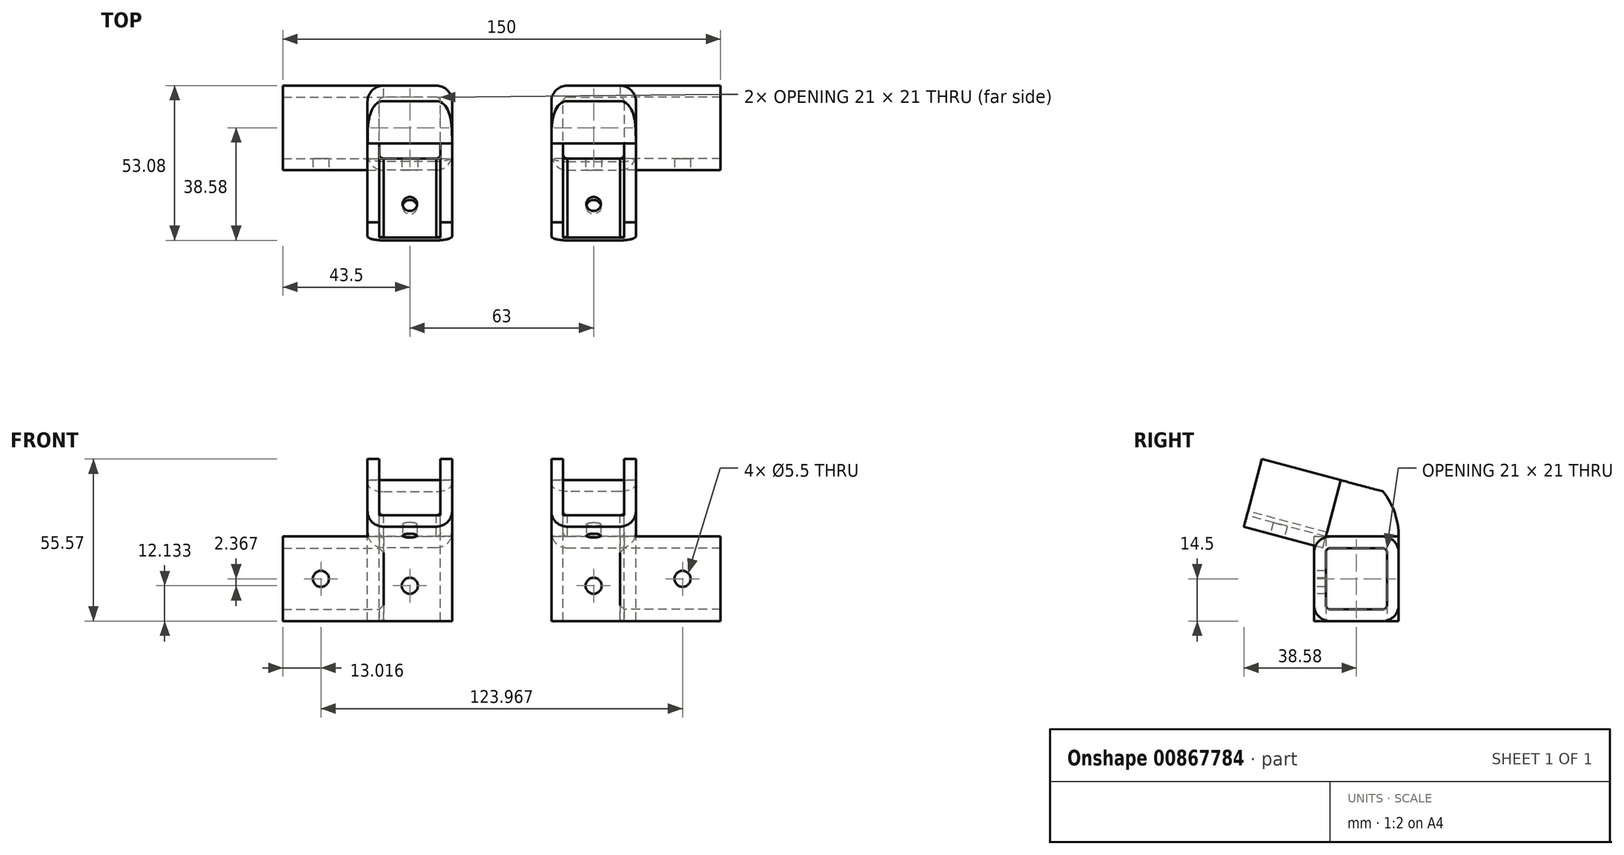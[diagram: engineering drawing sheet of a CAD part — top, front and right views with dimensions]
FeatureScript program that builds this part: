
annotation { "Feature Type Name" : "Feature", "Feature Type Description" : "" }
export const myFeature = defineFeature(function(context is Context, id is Id, definition is map)
    precondition{}
    {
        {
            var Q0;
            Q0=qCreatedBy(makeId("Top.planeOp"),FACE);
            var sketch = newSketch(context, id + "F0", { "sketchPlane" : qUnion([Q0])});
            skLineSegment(sketch, "E0.bottom", {"start": v(1.5, 0) * mm, "end": v(19.5, 0) * mm});
            skLineSegment(sketch, "E0.top", {"start": v(1.5, 21) * mm, "end": v(19.5, 21) * mm});
            skLineSegment(sketch, "E0.left", {"start": v(0, 1.5) * mm, "end": v(0, 19.5) * mm});
            skLineSegment(sketch, "E0.right", {"start": v(21, 1.5) * mm, "end": v(21, 19.5) * mm});
            skPoint(sketch, "E1.visualSharp", {"position": v(21, 21) * mm});
            skArc(sketch, "E1.filletArc", {"start": v(21, 19.5) * mm, "mid": v(20.56, 20.56) * mm, "end": v(19.5, 21) * mm});
            skPoint(sketch, "E2.visualSharp", {"position": v(21, 0) * mm});
            skArc(sketch, "E2.filletArc", {"start": v(19.5, 0) * mm, "mid": v(20.56, 0.44) * mm, "end": v(21, 1.5) * mm});
            skPoint(sketch, "E3.visualSharp", {"position": v(0, 0) * mm});
            skArc(sketch, "E3.filletArc", {"start": v(0, 1.5) * mm, "mid": v(0.44, 0.44) * mm, "end": v(1.5, 0) * mm});
            skPoint(sketch, "E4.visualSharp", {"position": v(0, 21) * mm});
            skArc(sketch, "E4.filletArc", {"start": v(1.5, 21) * mm, "mid": v(0.44, 20.56) * mm, "end": v(0, 19.5) * mm});
            skArc(sketch, "E5.0", {"start": v(19.5, -4) * mm, "mid": v(23.39, -2.39) * mm, "end": v(25, 1.5) * mm});
            skLineSegment(sketch, "E5.1", {"start": v(1.5, -4) * mm, "end": v(19.5, -4) * mm});
            skLineSegment(sketch, "E5.2", {"start": v(25, 1.5) * mm, "end": v(25, 19.5) * mm});
            skArc(sketch, "E5.3", {"start": v(-4, 1.5) * mm, "mid": v(-2.39, -2.39) * mm, "end": v(1.5, -4) * mm});
            skArc(sketch, "E5.4", {"start": v(25, 19.5) * mm, "mid": v(23.39, 23.39) * mm, "end": v(19.5, 25) * mm});
            skLineSegment(sketch, "E5.5", {"start": v(1.5, 25) * mm, "end": v(19.5, 25) * mm});
            skArc(sketch, "E5.6", {"start": v(1.5, 25) * mm, "mid": v(-2.39, 23.39) * mm, "end": v(-4, 19.5) * mm});
            skLineSegment(sketch, "E5.7", {"start": v(-4, 1.5) * mm, "end": v(-4, 19.5) * mm});
            skSolve(sketch);
        }
        {
            var Q0;
            Q0=makeQuery(id+"F0.imprint","IMPRINT",FACE,{"disambiguationData":[TD([[makeQuery(id+"F0.imprint","IMPRINT",EDGE,{"derivedFrom":sQuery(id+"F0.wireOp",EDGE,"E0.bottom")}),-1.0]])]});
            extrude(context, id + "F1", {"entities" : qUnion([Q0]), "oppositeDirection" : true, "depth" : 29 * mm, "offsetDistance" : 25 * mm});
        }
        {
            var Q0;
            Q0=qCreatedBy(makeId("Right.planeOp"),FACE);
            var sketch = newSketch(context, id + "F2", { "sketchPlane" : qUnion([Q0])});
            skLineSegment(sketch, "E6", {"start": v(0, 0) * mm, "end": v(-27.05, 7.25) * mm});
            skLineSegment(sketch, "E7", {"start": v(-27.05, 7.25) * mm, "end": v(-21.87, 26.57) * mm});
            skLineSegment(sketch, "E8", {"start": v(-21.87, 26.57) * mm, "end": v(5.18, 19.32) * mm});
            skLineSegment(sketch, "E9", {"start": v(5.18, 19.32) * mm, "end": v(0, 0) * mm});
            skSolve(sketch);
        }
        {
            var Q0;
            Q0=makeQuery(id+"F2.imprint","IMPRINT",FACE,{"disambiguationData":[TD([[makeQuery(id+"F2.imprint","IMPRINT",EDGE,{"derivedFrom":sQuery(id+"F2.wireOp",EDGE,"E6")}),-1.0]])]});
            extrude(context, id + "F3", {"entities" : qUnion([Q0]), "depth" : 21 * mm, "offsetDistance" : 25 * mm});
        }
        {
            var Q0;
            Q0=makeQuery(id+"F3.opExtrude","SWEPT_FACE",FACE,{"disambiguationData":[OSD([sQuery(id+"F2.wireOp",EDGE,"E7")])]});
            var sketch = newSketch(context, id + "F4", { "sketchPlane" : qUnion([Q0])});
            skLineSegment(sketch, "E10", {"start": v(0, 20) * mm, "end": v(0, 1.5) * mm});
            skLineSegment(sketch, "E11", {"start": v(1.5, 0) * mm, "end": v(19.5, 0) * mm});
            skLineSegment(sketch, "E12", {"start": v(21, 1.5) * mm, "end": v(21, 20) * mm});
            skPoint(sketch, "E13.visualSharp", {"position": v(0, 0) * mm});
            skArc(sketch, "E13.filletArc", {"start": v(0, 1.5) * mm, "mid": v(0.44, 0.44) * mm, "end": v(1.5, 0) * mm});
            skPoint(sketch, "E14.visualSharp", {"position": v(21, 0) * mm});
            skArc(sketch, "E14.filletArc", {"start": v(19.5, 0) * mm, "mid": v(20.56, 0.44) * mm, "end": v(21, 1.5) * mm});
            skLineSegment(sketch, "E15.0", {"start": v(25, 1.5) * mm, "end": v(25, 20) * mm});
            skLineSegment(sketch, "E15.1", {"start": v(-4, 20) * mm, "end": v(-4, 1.5) * mm});
            skArc(sketch, "E15.2", {"start": v(-4, 1.5) * mm, "mid": v(-2.39, -2.39) * mm, "end": v(1.5, -4) * mm});
            skLineSegment(sketch, "E15.3", {"start": v(1.5, -4) * mm, "end": v(19.5, -4) * mm});
            skArc(sketch, "E15.4", {"start": v(19.5, -4) * mm, "mid": v(23.39, -2.39) * mm, "end": v(25, 1.5) * mm});
            skLineSegment(sketch, "E16", {"start": v(-4, 20) * mm, "end": v(0, 20) * mm});
            skLineSegment(sketch, "E17", {"start": v(21, 20) * mm, "end": v(25, 20) * mm});
            skSolve(sketch);
        }
        {
            var Q0;
            {var subQ0=sQuery(id+"F4.wireOp",EDGE,"E10");Q0=makeQuery(id+"F4.imprint","IMPRINT",FACE,{"disambiguationData":[TD([[makeQuery(id+"F4.imprint","IMPRINT",EDGE,{"derivedFrom":subQ0}),1.0]])]});}
            extrude(context, id + "F5", {"entities" : qUnion([Q0]), "oppositeDirection" : true, "depth" : 28 * mm, "offsetDistance" : 25 * mm});
        }
        {
            var Q0;
            Q0=makeQuery(id+"F5.opExtrude","CAP_FACE",FACE,{"disambiguationData":[OSD([sQuery(id+"F2.wireOp",EDGE,"E6"),sQuery(id+"F2.wireOp",EDGE,"E7"),sQuery(id+"F4.wireOp",EDGE,"E10"),sQuery(id+"F4.wireOp",EDGE,"E11"),sQuery(id+"F4.wireOp",EDGE,"E12"),sQuery(id+"F4.wireOp",EDGE,"E15.0"),sQuery(id+"F4.wireOp",EDGE,"E15.1"),sQuery(id+"F4.wireOp",EDGE,"E15.2"),sQuery(id+"F4.wireOp",EDGE,"E15.3"),sQuery(id+"F4.wireOp",EDGE,"E15.4"),sQuery(id+"F4.wireOp",EDGE,"E16"),sQuery(id+"F4.wireOp",EDGE,"E17")])],"isStart":true});
            var sketch = newSketch(context, id + "F6", { "sketchPlane" : qUnion([Q0])});
            skLineSegment(sketch, "E18.bottom", {"start": v(0, 20) * mm, "end": v(21, 20) * mm});
            skLineSegment(sketch, "E18.top", {"start": v(1.5, 0) * mm, "end": v(19.5, 0) * mm});
            skLineSegment(sketch, "E18.left", {"start": v(0, 20) * mm, "end": v(0, 1.5) * mm});
            skLineSegment(sketch, "E18.right", {"start": v(21, 20) * mm, "end": v(21, 1.5) * mm});
            skPoint(sketch, "E19.visualSharp", {"position": v(0, 0) * mm});
            skArc(sketch, "E19.filletArc", {"start": v(0, 1.5) * mm, "mid": v(0.44, 0.44) * mm, "end": v(1.5, 0) * mm});
            skPoint(sketch, "E20.visualSharp", {"position": v(21, 0) * mm});
            skArc(sketch, "E20.filletArc", {"start": v(19.5, 0) * mm, "mid": v(20.56, 0.44) * mm, "end": v(21, 1.5) * mm});
            skSolve(sketch);
        }
        {
            var Q0;
            Q0=makeQuery(id+"F6.imprint","IMPRINT",FACE,{"disambiguationData":[TD([[makeQuery(id+"F6.imprint","IMPRINT",EDGE,{"derivedFrom":sQuery(id+"F6.wireOp",EDGE,"E18.bottom")}),-1.0]])]});
            extrude(context, id + "F7", {"entities" : qUnion([Q0]), "operationType" : NewBodyOperationType.REMOVE, "oppositeDirection" : true, "depth" : 28 * mm, "offsetDistance" : 25 * mm});
        }
        {
            var Q0;
            Q0=makeQuery(id+"F1.opExtrude","CAP_FACE",FACE,{"disambiguationData":[OSD([sQuery(id+"F0.wireOp",EDGE,"E0.bottom"),sQuery(id+"F0.wireOp",EDGE,"E0.top"),sQuery(id+"F0.wireOp",EDGE,"E0.left"),sQuery(id+"F0.wireOp",EDGE,"E0.right"),sQuery(id+"F0.wireOp",EDGE,"E1.filletArc"),sQuery(id+"F0.wireOp",EDGE,"E2.filletArc"),sQuery(id+"F0.wireOp",EDGE,"E3.filletArc"),sQuery(id+"F0.wireOp",EDGE,"E4.filletArc"),sQuery(id+"F0.wireOp",EDGE,"E5.0"),sQuery(id+"F0.wireOp",EDGE,"E5.1"),sQuery(id+"F0.wireOp",EDGE,"E5.2"),sQuery(id+"F0.wireOp",EDGE,"E5.3"),sQuery(id+"F0.wireOp",EDGE,"E5.4"),sQuery(id+"F0.wireOp",EDGE,"E5.5"),sQuery(id+"F0.wireOp",EDGE,"E5.6"),sQuery(id+"F0.wireOp",EDGE,"E5.7")])],"isStart":true});
            var sketch = newSketch(context, id + "F8", { "sketchPlane" : qUnion([Q0])});
            skLineSegment(sketch, "E21.bottom", {"start": v(1.5, 21) * mm, "end": v(19.5, 21) * mm});
            skLineSegment(sketch, "E21.top", {"start": v(1.5, 0) * mm, "end": v(19.5, 0) * mm});
            skLineSegment(sketch, "E21.left", {"start": v(0, 19.5) * mm, "end": v(0, 1.5) * mm});
            skLineSegment(sketch, "E21.right", {"start": v(21, 19.5) * mm, "end": v(21, 1.5) * mm});
            skPoint(sketch, "E22.visualSharp", {"position": v(21, 21) * mm});
            skArc(sketch, "E22.filletArc", {"start": v(21, 19.5) * mm, "mid": v(20.56, 20.56) * mm, "end": v(19.5, 21) * mm});
            skPoint(sketch, "E23.visualSharp", {"position": v(0, 21) * mm});
            skArc(sketch, "E23.filletArc", {"start": v(1.5, 21) * mm, "mid": v(0.44, 20.56) * mm, "end": v(0, 19.5) * mm});
            skPoint(sketch, "E24.visualSharp", {"position": v(0, 0) * mm});
            skArc(sketch, "E24.filletArc", {"start": v(0, 1.5) * mm, "mid": v(0.44, 0.44) * mm, "end": v(1.5, 0) * mm});
            skPoint(sketch, "E25.visualSharp", {"position": v(21, 0) * mm});
            skArc(sketch, "E25.filletArc", {"start": v(19.5, 0) * mm, "mid": v(20.56, 0.44) * mm, "end": v(21, 1.5) * mm});
            skArc(sketch, "E26.0", {"start": v(19.5, -4) * mm, "mid": v(23.39, -2.39) * mm, "end": v(25, 1.5) * mm});
            skLineSegment(sketch, "E26.1", {"start": v(25, 19.5) * mm, "end": v(25, 1.5) * mm});
            skArc(sketch, "E26.2", {"start": v(25, 19.5) * mm, "mid": v(23.39, 23.39) * mm, "end": v(19.5, 25) * mm});
            skArc(sketch, "E26.3", {"start": v(-4, 1.5) * mm, "mid": v(-2.39, -2.39) * mm, "end": v(1.5, -4) * mm});
            skLineSegment(sketch, "E26.4", {"start": v(-4, 19.5) * mm, "end": v(-4, 1.5) * mm});
            skArc(sketch, "E26.5", {"start": v(1.5, 25) * mm, "mid": v(-2.39, 23.39) * mm, "end": v(-4, 19.5) * mm});
            skLineSegment(sketch, "E26.6", {"start": v(1.5, 25) * mm, "end": v(19.5, 25) * mm});
            skLineSegment(sketch, "E27", {"start": v(24.8, 0) * mm, "end": v(-3.8, 0) * mm});
            skSolve(sketch);
        }
        {
            var Q0;
            Q0=makeQuery(id+"F8.imprint","IMPRINT",FACE,{"disambiguationData":[TD([[makeQuery(id+"F8.imprint","IMPRINT",EDGE,{"derivedFrom":sQuery(id+"F8.wireOp",EDGE,"E21.bottom")}),1.0]])]});
            var Q1;
            Q1=makeQuery(id+"F8.imprint","IMPRINT",FACE,{"disambiguationData":[TD([[makeQuery(id+"F8.imprint","IMPRINT",EDGE,{"derivedFrom":sQuery(id+"F8.wireOp",EDGE,"E21.bottom")}),-1.0]])]});
            var Q2;
            Q2=sQuery(id+"F8.wireOp",EDGE,"E21.top");
            revolve(context, id + "F9", {"surfaceOperationType" : NewSurfaceOperationType.NEW, "entities" : qUnion([Q0, Q1]), "axis" : qUnion([Q2]), "revolveType" : RevolveType.ONE_DIRECTION, "angle" : 75 * degree});
        }
        {
            var Q0;
            Q0=makeQuery(id+"F9.opRevolve","SWEPT_FACE",FACE,{"disambiguationData":[OSD([sQuery(id+"F8.wireOp",EDGE,"E26.4")])]});
            var sketch = newSketch(context, id + "F10", { "sketchPlane" : qUnion([Q0])});
            skLineSegment(sketch, "E28", {"start": v(-5.05, 18.84) * mm, "end": v(-5.18, 19.32) * mm});
            skLineSegment(sketch, "E29", {"start": v(-5.18, 19.32) * mm, "end": v(-21.6, 14.92) * mm});
            skLineSegment(sketch, "E30", {"start": v(-21.6, 14.92) * mm, "end": v(-23.5, 23.3) * mm});
            skLineSegment(sketch, "E31", {"start": v(-23.5, 23.3) * mm, "end": v(-5.18, 24.55) * mm});
            skLineSegment(sketch, "E32", {"start": v(-5.18, 24.55) * mm, "end": v(-5.18, 19.32) * mm});
            skSolve(sketch);
        }
        {
            var Q0;
            Q0=makeQuery(id+"F10.imprint","IMPRINT",FACE,{"disambiguationData":[TD([[makeQuery(id+"F10.imprint","IMPRINT",EDGE,{"derivedFrom":sQuery(id+"F10.wireOp",EDGE,"E29")}),-1.0]])]});
            extrude(context, id + "F11", {"entities" : qUnion([Q0]), "operationType" : NewBodyOperationType.REMOVE, "oppositeDirection" : true, "depth" : 43.3 * mm, "offsetDistance" : 25 * mm});
        }
        {
            var Q0;
            Q0=makeQuery(id+"F1.opExtrude","SWEPT_FACE",FACE,{"disambiguationData":[OSD([sQuery(id+"F0.wireOp",EDGE,"E5.1")])]});
            var sketch = newSketch(context, id + "F12", { "sketchPlane" : qUnion([Q0])});
            skCircle(sketch, "E33", {"center": v(10.5, -16.87) * mm, "radius": 2.75 * mm});
            skPoint(sketch, "E33.centerSnap0", {"position": v(10.5, -29) * mm});
            skSolve(sketch);
        }
        {
            var Q0;
            Q0=makeQuery(id+"F12.imprint","IMPRINT",FACE,{"disambiguationData":[TD([[makeQuery(id+"F12.imprint","IMPRINT",EDGE,{"derivedFrom":sQuery(id+"F12.wireOp",EDGE,"E33")}),1.0]])]});
            extrude(context, id + "F13", {"entities" : qUnion([Q0]), "operationType" : NewBodyOperationType.REMOVE, "oppositeDirection" : true, "depth" : 5 * mm, "offsetDistance" : 25 * mm});
        }
        {
            var Q0;
            Q0=makeQuery(id+"F5.opExtrude","SWEPT_FACE",FACE,{"disambiguationData":[OSD([sQuery(id+"F4.wireOp",EDGE,"E15.3")])]});
            var sketch = newSketch(context, id + "F14", { "sketchPlane" : qUnion([Q0])});
            skCircle(sketch, "E34", {"center": v(10.5, 16.15) * mm, "radius": 2.5 * mm});
            skPoint(sketch, "E34.centerSnap0", {"position": v(10.5, 28) * mm});
            skSolve(sketch);
        }
        {
            var Q0;
            Q0=makeQuery(id+"F14.imprint","IMPRINT",FACE,{"disambiguationData":[TD([[makeQuery(id+"F14.imprint","IMPRINT",EDGE,{"derivedFrom":sQuery(id+"F14.wireOp",EDGE,"E34")}),1.0]])]});
            extrude(context, id + "F15", {"entities" : qUnion([Q0]), "operationType" : NewBodyOperationType.REMOVE, "oppositeDirection" : true, "depth" : 5 * mm, "offsetDistance" : 25 * mm});
        }
        {
            var Q0;
            Q0=makeQuery(id+"F1.opExtrude","SWEPT_FACE",FACE,{"disambiguationData":[OSD([sQuery(id+"F0.wireOp",EDGE,"E5.2")])]});
            var sketch = newSketch(context, id + "F16", { "sketchPlane" : qUnion([Q0])});
            skLineSegment(sketch, "E35", {"start": v(1.5, -29) * mm, "end": v(-4, -29) * mm});
            skLineSegment(sketch, "E36", {"start": v(-4, -29) * mm, "end": v(-4, -29) * mm});
            skLineSegment(sketch, "E37.bottom", {"start": v(1.5, -29) * mm, "end": v(19.5, -29) * mm});
            skLineSegment(sketch, "E37.top", {"start": v(1.5, 0) * mm, "end": v(19.5, 0) * mm});
            skLineSegment(sketch, "E37.left", {"start": v(-4, -23.5) * mm, "end": v(-4, -5.5) * mm});
            skLineSegment(sketch, "E37.right", {"start": v(25, -23.5) * mm, "end": v(25, -5.5) * mm});
            skPoint(sketch, "E38.visualSharp", {"position": v(-4, 0) * mm});
            skArc(sketch, "E38.filletArc", {"start": v(1.5, 0) * mm, "mid": v(-2.39, -1.61) * mm, "end": v(-4, -5.5) * mm});
            skPoint(sketch, "E39.visualSharp", {"position": v(25, 0) * mm});
            skArc(sketch, "E39.filletArc", {"start": v(25, -5.5) * mm, "mid": v(23.39, -1.61) * mm, "end": v(19.5, 0) * mm});
            skPoint(sketch, "E40.visualSharp", {"position": v(25, -29) * mm});
            skArc(sketch, "E40.filletArc", {"start": v(19.5, -29) * mm, "mid": v(23.39, -27.39) * mm, "end": v(25, -23.5) * mm});
            skPoint(sketch, "E41.visualSharp", {"position": v(-4, -29) * mm});
            skArc(sketch, "E41.filletArc", {"start": v(-4, -23.5) * mm, "mid": v(-2.39, -27.39) * mm, "end": v(1.5, -29) * mm});
            skLineSegment(sketch, "E42.0", {"start": v(1.5, -4) * mm, "end": v(19.5, -4) * mm});
            skArc(sketch, "E42.1", {"start": v(21, -5.5) * mm, "mid": v(20.56, -4.44) * mm, "end": v(19.5, -4) * mm});
            skArc(sketch, "E42.2", {"start": v(1.5, -4) * mm, "mid": v(0.44, -4.44) * mm, "end": v(0, -5.5) * mm});
            skLineSegment(sketch, "E42.3", {"start": v(21, -23.5) * mm, "end": v(21, -5.5) * mm});
            skLineSegment(sketch, "E42.4", {"start": v(0, -23.5) * mm, "end": v(0, -5.5) * mm});
            skArc(sketch, "E42.5", {"start": v(0, -23.5) * mm, "mid": v(0.44, -24.56) * mm, "end": v(1.5, -25) * mm});
            skLineSegment(sketch, "E42.6", {"start": v(1.5, -25) * mm, "end": v(19.5, -25) * mm});
            skArc(sketch, "E42.7", {"start": v(19.5, -25) * mm, "mid": v(20.56, -24.56) * mm, "end": v(21, -23.5) * mm});
            skSolve(sketch);
        }
        {
            var Q0;
            Q0=makeQuery(id+"F16.imprint","IMPRINT",FACE,{"disambiguationData":[TD([[makeQuery(id+"F16.imprint","IMPRINT",EDGE,{"derivedFrom":sQuery(id+"F16.wireOp",EDGE,"E37.top")}),-1.0]])]});
            var Q1;
            {var subQ0=sQuery(id+"F16.wireOp",EDGE,"E37.bottom");Q1=makeQuery(id+"F16.imprint","IMPRINT",FACE,{"disambiguationData":[TD([[makeQuery(id+"F16.imprint","IMPRINT",EDGE,{"derivedFrom":subQ0}),1.0]])]});}
            var Q2;
            {var subQ0=sQuery(id+"F16.wireOp",EDGE,"E42.0");Q2=makeQuery(id+"F16.imprint","IMPRINT",FACE,{"disambiguationData":[TD([[makeQuery(id+"F16.imprint","IMPRINT",EDGE,{"derivedFrom":subQ0}),1.0]])]});}
            var Q3;
            Q3=makeQuery(id+"F16.imprint","IMPRINT",FACE,{"disambiguationData":[TD([[makeQuery(id+"F16.imprint","IMPRINT",EDGE,{"derivedFrom":sQuery(id+"F16.wireOp",EDGE,"E37.left")}),-1.0]])]});
            var Q4;
            Q4=makeQuery(id+"F16.imprint","IMPRINT",FACE,{"disambiguationData":[TD([[makeQuery(id+"F16.imprint","IMPRINT",EDGE,{"derivedFrom":sQuery(id+"F16.wireOp",EDGE,"E37.right")}),1.0]])]});
            extrude(context, id + "F17", {"entities" : qUnion([Q0, Q1, Q2, Q3, Q4]), "endBound" : BoundingType.SYMMETRIC, "depth" : 11 * mm, "offsetDistance" : 25 * mm});
        }
        {
            var Q0;
            Q0=makeQuery(id+"F17.opExtrude","SWEPT_FACE",FACE,{"disambiguationData":[OSD([sQuery(id+"F16.wireOp",EDGE,"E37.bottom")])]});
            var sketch = newSketch(context, id + "F18", { "sketchPlane" : qUnion([Q0])});
            skLineSegment(sketch, "E43", {"start": v(19.5, 0) * mm, "end": v(19.5, -21) * mm});
            skLineSegment(sketch, "E44", {"start": v(19.5, -21) * mm, "end": v(19.5, -21) * mm});
            skLineSegment(sketch, "E45", {"start": v(21, -19.5) * mm, "end": v(21, -1.5) * mm});
            skLineSegment(sketch, "E46", {"start": v(19.5, 0) * mm, "end": v(19.5, 0) * mm});
            skPoint(sketch, "E47.visualSharp", {"position": v(21, -21) * mm});
            skArc(sketch, "E47.filletArc", {"start": v(19.5, -21) * mm, "mid": v(20.56, -20.56) * mm, "end": v(21, -19.5) * mm});
            skPoint(sketch, "E48.visualSharp", {"position": v(21, 0) * mm});
            skArc(sketch, "E48.filletArc", {"start": v(21, -1.5) * mm, "mid": v(20.56, -0.44) * mm, "end": v(19.5, 0) * mm});
            skSolve(sketch);
        }
        {
            var Q0;
            {var subQ3=sQuery(id+"F18.wireOp",EDGE,"E48.filletArc");Q0=makeQuery(id+"F18.imprint","IMPRINT",FACE,{"disambiguationData":[TD([[makeQuery(id+"F18.imprint","IMPRINT",EDGE,{"derivedFrom":subQ3}),1.0]])]});}
            var Q1;
            {var subQ7=sQuery(id+"F18.wireOp",EDGE,"E45");Q1=makeQuery(id+"F18.imprint","IMPRINT",FACE,{"disambiguationData":[TD([[makeQuery(id+"F18.imprint","IMPRINT",EDGE,{"derivedFrom":subQ7}),1.0]])]});}
            var Q2;
            {var subQ3=sQuery(id+"F18.wireOp",EDGE,"E47.filletArc");Q2=makeQuery(id+"F18.imprint","IMPRINT",FACE,{"disambiguationData":[TD([[makeQuery(id+"F18.imprint","IMPRINT",EDGE,{"derivedFrom":subQ3}),1.0]])]});}
            extrude(context, id + "F19", {"entities" : qUnion([Q0, Q1, Q2]), "operationType" : NewBodyOperationType.REMOVE, "oppositeDirection" : true, "depth" : 29 * mm, "offsetDistance" : 25 * mm});
        }
        {
            var Q0;
            Q0=makeQuery(id+"F17.opExtrude","CAP_FACE",FACE,{"disambiguationData":[OSD([sQuery(id+"F16.wireOp",EDGE,"E37.bottom"),sQuery(id+"F16.wireOp",EDGE,"E37.top"),sQuery(id+"F16.wireOp",EDGE,"E37.left"),sQuery(id+"F16.wireOp",EDGE,"E37.right"),sQuery(id+"F16.wireOp",EDGE,"E38.filletArc"),sQuery(id+"F16.wireOp",EDGE,"E39.filletArc"),sQuery(id+"F16.wireOp",EDGE,"E40.filletArc"),sQuery(id+"F16.wireOp",EDGE,"E41.filletArc"),sQuery(id+"F16.wireOp",EDGE,"E42.0"),sQuery(id+"F16.wireOp",EDGE,"E42.1"),sQuery(id+"F16.wireOp",EDGE,"E42.2"),sQuery(id+"F16.wireOp",EDGE,"E42.3"),sQuery(id+"F16.wireOp",EDGE,"E42.4"),sQuery(id+"F16.wireOp",EDGE,"E42.5"),sQuery(id+"F16.wireOp",EDGE,"E42.6"),sQuery(id+"F16.wireOp",EDGE,"E42.7")])],"isStart":false});
            var sketch = newSketch(context, id + "F20", { "sketchPlane" : qUnion([Q0])});
            skLineSegment(sketch, "E49", {"start": v(1.5, -25) * mm, "end": v(19.5, -25) * mm});
            skLineSegment(sketch, "E50", {"start": v(21, -23.5) * mm, "end": v(21, -5.5) * mm});
            skLineSegment(sketch, "E51", {"start": v(19.5, -4) * mm, "end": v(1.5, -4) * mm});
            skLineSegment(sketch, "E52", {"start": v(0, -5.5) * mm, "end": v(0, -23.5) * mm});
            skLineSegment(sketch, "E53", {"start": v(1.5, -25) * mm, "end": v(1.5, -25) * mm});
            skPoint(sketch, "E54.visualSharp", {"position": v(0, -4) * mm});
            skArc(sketch, "E54.filletArc", {"start": v(1.5, -4) * mm, "mid": v(0.44, -4.44) * mm, "end": v(0, -5.5) * mm});
            skPoint(sketch, "E55.visualSharp", {"position": v(21, -4) * mm});
            skArc(sketch, "E55.filletArc", {"start": v(21, -5.5) * mm, "mid": v(20.56, -4.44) * mm, "end": v(19.5, -4) * mm});
            skPoint(sketch, "E56.visualSharp", {"position": v(21, -25) * mm});
            skArc(sketch, "E56.filletArc", {"start": v(19.5, -25) * mm, "mid": v(20.56, -24.56) * mm, "end": v(21, -23.5) * mm});
            skPoint(sketch, "E57.visualSharp", {"position": v(0, -25) * mm});
            skArc(sketch, "E57.filletArc", {"start": v(0, -23.5) * mm, "mid": v(0.44, -24.56) * mm, "end": v(1.5, -25) * mm});
            skArc(sketch, "E58.0", {"start": v(25, -5.5) * mm, "mid": v(23.39, -1.61) * mm, "end": v(19.5, 0) * mm});
            skLineSegment(sketch, "E58.1", {"start": v(25, -23.5) * mm, "end": v(25, -5.5) * mm});
            skLineSegment(sketch, "E58.2", {"start": v(19.5, 0) * mm, "end": v(1.5, 0) * mm});
            skArc(sketch, "E58.3", {"start": v(19.5, -29) * mm, "mid": v(23.39, -27.39) * mm, "end": v(25, -23.5) * mm});
            skArc(sketch, "E58.4", {"start": v(1.5, 0) * mm, "mid": v(-2.39, -1.61) * mm, "end": v(-4, -5.5) * mm});
            skLineSegment(sketch, "E58.5", {"start": v(-4, -5.5) * mm, "end": v(-4, -23.5) * mm});
            skArc(sketch, "E58.6", {"start": v(-4, -23.5) * mm, "mid": v(-2.39, -27.39) * mm, "end": v(1.5, -29) * mm});
            skLineSegment(sketch, "E58.7", {"start": v(1.5, -29) * mm, "end": v(19.5, -29) * mm});
            skSolve(sketch);
        }
        {
            var Q0;
            Q0=makeQuery(id+"F20.imprint","IMPRINT",FACE,{"disambiguationData":[TD([[makeQuery(id+"F20.imprint","IMPRINT",EDGE,{"derivedFrom":sQuery(id+"F20.wireOp",EDGE,"E49")}),-1.0]])]});
            extrude(context, id + "F21", {"entities" : qUnion([Q0]), "operationType" : NewBodyOperationType.ADD, "depth" : 23.5 * mm, "offsetDistance" : 25 * mm});
        }
        {
            var Q0;
            Q0=makeQuery(id+"F21.boolean.opBoolean","MERGE",FACE,{"derivedFrom":[makeQuery(id+"F17.opExtrude","SWEPT_FACE",FACE,{"disambiguationData":[OSD([sQuery(id+"F16.wireOp",EDGE,"E37.left")])]}),makeQuery(id+"F21.opExtrude","SWEPT_FACE",FACE,{"disambiguationData":[OSD([sQuery(id+"F20.wireOp",EDGE,"E58.5")])]})]});
            var sketch = newSketch(context, id + "F22", { "sketchPlane" : qUnion([Q0])});
            skCircle(sketch, "E59", {"center": v(40.98, -14.5) * mm, "radius": 2.75 * mm});
            skPoint(sketch, "E59.centerSnap0", {"position": v(54, -14.5) * mm});
            skSolve(sketch);
        }
        {
            var Q0;
            Q0=makeQuery(id+"F22.imprint","IMPRINT",FACE,{"disambiguationData":[TD([[makeQuery(id+"F22.imprint","IMPRINT",EDGE,{"derivedFrom":sQuery(id+"F22.wireOp",EDGE,"E59")}),1.0]])]});
            extrude(context, id + "F23", {"entities" : qUnion([Q0]), "operationType" : NewBodyOperationType.REMOVE, "oppositeDirection" : true, "depth" : 15.2 * mm, "offsetDistance" : 25 * mm});
        }
        {
            var Q0;
            Q0=qCreatedBy(makeId("Right.planeOp"),FACE);
            cPlane(context, id + "F24", {"entities" : qUnion([Q0]), "cplaneType" : CPlaneType.OFFSET, "offset" : 21 * mm, "oppositeDirection" : true, "width" : 150 * mm, "height" : 150 * mm});
        }
        {
            var Q0;
            Q0=makeQuery(id+"F9.opRevolve","SWEPT_BODY",BODY,{"disambiguationData":[OSD([sQuery(id+"F8.wireOp",EDGE,"E21.top"),sQuery(id+"F8.wireOp",EDGE,"E26.0"),sQuery(id+"F8.wireOp",EDGE,"E26.1"),sQuery(id+"F8.wireOp",EDGE,"E26.2"),sQuery(id+"F8.wireOp",EDGE,"E26.3"),sQuery(id+"F8.wireOp",EDGE,"E26.4"),sQuery(id+"F8.wireOp",EDGE,"E26.5"),sQuery(id+"F8.wireOp",EDGE,"E26.6"),sQuery(id+"F8.wireOp",EDGE,"E27")])]});
            var Q1;
            Q1=makeQuery(id+"F7.boolean.opBoolean","SPLIT",BODY,{"disambiguationData":[OD(1.0)],"derivedFrom":makeQuery(id+"F3.opExtrude","SWEPT_BODY",BODY,{"disambiguationData":[OSD([sQuery(id+"F2.wireOp",EDGE,"E6"),sQuery(id+"F2.wireOp",EDGE,"E7"),sQuery(id+"F2.wireOp",EDGE,"E8"),sQuery(id+"F2.wireOp",EDGE,"E9")])]})});
            var Q2;
            Q2=makeQuery(id+"F17.opExtrude","SWEPT_BODY",BODY,{"disambiguationData":[OSD([sQuery(id+"F16.wireOp",EDGE,"E37.bottom"),sQuery(id+"F16.wireOp",EDGE,"E37.top"),sQuery(id+"F16.wireOp",EDGE,"E37.left"),sQuery(id+"F16.wireOp",EDGE,"E37.right"),sQuery(id+"F16.wireOp",EDGE,"E38.filletArc"),sQuery(id+"F16.wireOp",EDGE,"E39.filletArc"),sQuery(id+"F16.wireOp",EDGE,"E40.filletArc"),sQuery(id+"F16.wireOp",EDGE,"E41.filletArc"),sQuery(id+"F16.wireOp",EDGE,"E42.0"),sQuery(id+"F16.wireOp",EDGE,"E42.1"),sQuery(id+"F16.wireOp",EDGE,"E42.2"),sQuery(id+"F16.wireOp",EDGE,"E42.3"),sQuery(id+"F16.wireOp",EDGE,"E42.4"),sQuery(id+"F16.wireOp",EDGE,"E42.5"),sQuery(id+"F16.wireOp",EDGE,"E42.6"),sQuery(id+"F16.wireOp",EDGE,"E42.7")])]});
            var Q3;
            Q3=makeQuery(id+"F1.opExtrude","SWEPT_BODY",BODY,{"disambiguationData":[OSD([sQuery(id+"F0.wireOp",EDGE,"E0.bottom"),sQuery(id+"F0.wireOp",EDGE,"E0.top"),sQuery(id+"F0.wireOp",EDGE,"E0.left"),sQuery(id+"F0.wireOp",EDGE,"E0.right"),sQuery(id+"F0.wireOp",EDGE,"E1.filletArc"),sQuery(id+"F0.wireOp",EDGE,"E2.filletArc"),sQuery(id+"F0.wireOp",EDGE,"E3.filletArc"),sQuery(id+"F0.wireOp",EDGE,"E4.filletArc"),sQuery(id+"F0.wireOp",EDGE,"E5.0"),sQuery(id+"F0.wireOp",EDGE,"E5.1"),sQuery(id+"F0.wireOp",EDGE,"E5.2"),sQuery(id+"F0.wireOp",EDGE,"E5.3"),sQuery(id+"F0.wireOp",EDGE,"E5.4"),sQuery(id+"F0.wireOp",EDGE,"E5.5"),sQuery(id+"F0.wireOp",EDGE,"E5.6"),sQuery(id+"F0.wireOp",EDGE,"E5.7")])]});
            var Q4;
            Q4=makeQuery(id+"F5.opExtrude","SWEPT_BODY",BODY,{"disambiguationData":[OSD([sQuery(id+"F2.wireOp",EDGE,"E6"),sQuery(id+"F2.wireOp",EDGE,"E7"),sQuery(id+"F4.wireOp",EDGE,"E10"),sQuery(id+"F4.wireOp",EDGE,"E11"),sQuery(id+"F4.wireOp",EDGE,"E12"),sQuery(id+"F4.wireOp",EDGE,"E15.0"),sQuery(id+"F4.wireOp",EDGE,"E15.1"),sQuery(id+"F4.wireOp",EDGE,"E15.2"),sQuery(id+"F4.wireOp",EDGE,"E15.3"),sQuery(id+"F4.wireOp",EDGE,"E15.4"),sQuery(id+"F4.wireOp",EDGE,"E16"),sQuery(id+"F4.wireOp",EDGE,"E17")])]});
            var Q5;
            Q5=makeQuery(id+"F7.boolean.opBoolean","SPLIT",BODY,{"disambiguationData":[OD(0.0)],"derivedFrom":makeQuery(id+"F3.opExtrude","SWEPT_BODY",BODY,{"disambiguationData":[OSD([sQuery(id+"F2.wireOp",EDGE,"E6"),sQuery(id+"F2.wireOp",EDGE,"E7"),sQuery(id+"F2.wireOp",EDGE,"E8"),sQuery(id+"F2.wireOp",EDGE,"E9")])]})});
            var Q6;
            Q6=qCreatedBy(id+"F24.planeOp",FACE);
            mirror(context, id + "F25", {"entities" : qUnion([Q0, Q1, Q2, Q3, Q4, Q5]), "mirrorPlane" : qUnion([Q6])});
        }
    });
